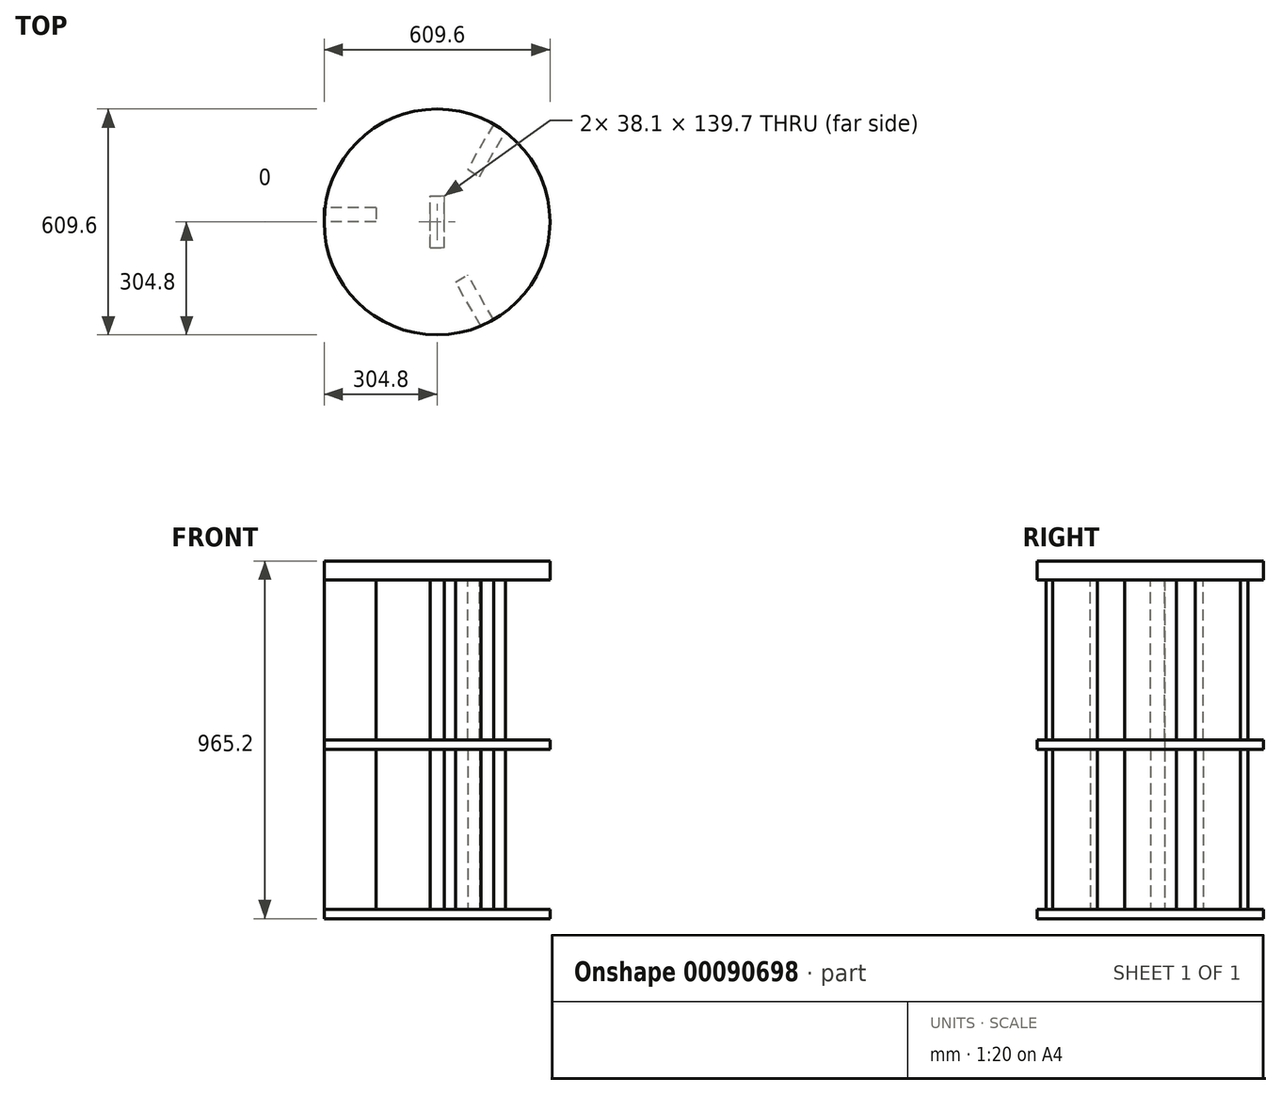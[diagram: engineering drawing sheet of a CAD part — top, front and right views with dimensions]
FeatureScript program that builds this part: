
annotation { "Feature Type Name" : "Feature", "Feature Type Description" : "" }
export const myFeature = defineFeature(function(context is Context, id is Id, definition is map)
    precondition{}
    {
        {
            var Q0;
            Q0=qCreatedBy(makeId("Top.planeOp"),FACE);
            var sketch = newSketch(context, id + "F0", { "sketchPlane" : qUnion([Q0])});
            skCircle(sketch, "E0", {"center": v(0, 0) * mm, "radius": 304.8 * mm});
            skSolve(sketch);
        }
        {
            var Q0;
            Q0 = qSketchRegion(id + "F0", true);
            extrude(context, id + "F1", {"entities" : qUnion([Q0]), "depth" : 25.4 * mm});
        }
        {
            var Q0;
            Q0=qCreatedBy(makeId("Top.planeOp"),FACE);
            cPlane(context, id + "F2", {"entities" : qUnion([Q0]), "cplaneType" : CPlaneType.OFFSET, "offset" : 457.2 * mm, "width" : 152.4 * mm, "height" : 152.4 * mm});
        }
        {
            var Q0;
            Q0=qCreatedBy(id+"F2.planeOp",FACE);
            var sketch = newSketch(context, id + "F3", { "sketchPlane" : qUnion([Q0])});
            skCircle(sketch, "E1", {"center": v(0, 0) * mm, "radius": 304.8 * mm});
            skSolve(sketch);
        }
        {
            var Q0;
            Q0=makeQuery(id+"F3.imprint","IMPRINT",FACE,{"disambiguationData":[TD([[makeQuery(id+"F3.imprint","IMPRINT",EDGE,{"derivedFrom":sQuery(id+"F3.wireOp",EDGE,"E1")}),1.0]])]});
            extrude(context, id + "F4", {"entities" : qUnion([Q0]), "depth" : 25.4 * mm});
        }
        {
            var Q0;
            Q0=qCreatedBy(id+"F2.planeOp",FACE);
            cPlane(context, id + "F5", {"entities" : qUnion([Q0]), "cplaneType" : CPlaneType.OFFSET, "offset" : 457.2 * mm, "width" : 152.4 * mm, "height" : 152.4 * mm});
        }
        {
            var Q0;
            Q0=qCreatedBy(id+"F5.planeOp",FACE);
            var sketch = newSketch(context, id + "F6", { "sketchPlane" : qUnion([Q0])});
            skCircle(sketch, "E2", {"center": v(0, 0) * mm, "radius": 304.8 * mm});
            skSolve(sketch);
        }
        {
            var Q0;
            Q0=makeQuery(id+"F1.opExtrude","CAP_FACE",FACE,{"disambiguationData":[OSD([sQuery(id+"F0.wireOp",EDGE,"E0")])],"isStart":false});
            var sketch = newSketch(context, id + "F7", { "sketchPlane" : qUnion([Q0])});
            skLineSegment(sketch, "E3.bottom", {"start": v(-304.8, 0) * mm, "end": v(-165.1, 0) * mm});
            skLineSegment(sketch, "E3.top", {"start": v(-304.8, 38.1) * mm, "end": v(-165.1, 38.1) * mm});
            skLineSegment(sketch, "E3.left", {"start": v(-304.8, 0) * mm, "end": v(-304.8, 38.1) * mm});
            skLineSegment(sketch, "E3.right", {"start": v(-165.1, 0) * mm, "end": v(-165.1, 38.1) * mm});
            skLineSegment(sketch, "E4", {"start": v(-304.8, 0) * mm, "end": v(0, 0) * mm, "construction": true});
            skLineSegment(sketch, "E5", {"start": v(0, 0) * mm, "end": v(152.4, 263.96) * mm, "construction": true});
            skLineSegment(sketch, "E6", {"start": v(0, 0) * mm, "end": v(152.4, -263.96) * mm, "construction": true});
            skLineSegment(sketch, "E7", {"start": v(82.55, 142.98) * mm, "end": v(152.4, 263.96) * mm});
            skLineSegment(sketch, "E8", {"start": v(184.14, 242.89) * mm, "end": v(114.3, 121.9) * mm});
            skLineSegment(sketch, "E9", {"start": v(114.3, 121.9) * mm, "end": v(82.55, 142.98) * mm});
            skLineSegment(sketch, "E10", {"start": v(152.4, 263.96) * mm, "end": v(184.14, 242.89) * mm});
            skLineSegment(sketch, "E11", {"start": v(82.55, -142.98) * mm, "end": v(49.55, -162.03) * mm});
            skLineSegment(sketch, "E12", {"start": v(49.55, -162.03) * mm, "end": v(118.2, -280.94) * mm});
            skLineSegment(sketch, "E13", {"start": v(118.2, -280.94) * mm, "end": v(152.4, -263.96) * mm});
            skLineSegment(sketch, "E14", {"start": v(82.55, -142.98) * mm, "end": v(152.4, -263.96) * mm});
            skLineSegment(sketch, "E15.bottom", {"start": v(19.05, 69.85) * mm, "end": v(-19.05, 69.85) * mm});
            skLineSegment(sketch, "E15.top", {"start": v(19.05, -69.85) * mm, "end": v(-19.05, -69.85) * mm});
            skLineSegment(sketch, "E15.left", {"start": v(19.05, 69.85) * mm, "end": v(19.05, -69.85) * mm});
            skLineSegment(sketch, "E15.right", {"start": v(-19.05, 69.85) * mm, "end": v(-19.05, -69.85) * mm});
            skPoint(sketch, "E15.middle", {"position": v(0, 0) * mm});
            skSolve(sketch);
        }
        {
            var Q0;
            Q0 = qSketchRegion(id + "F7", true);
            var Q1;
            Q1=makeQuery(id+"F4.opExtrude","CAP_FACE",FACE,{"disambiguationData":[OSD([sQuery(id+"F3.wireOp",EDGE,"E1")])],"isStart":true});
            extrude(context, id + "F8", {"entities" : qUnion([Q0]), "operationType" : NewBodyOperationType.ADD, "endBound" : BoundingType.UP_TO_SURFACE, "endBoundEntityFace" : qUnion([Q1]), "depth" : 25.4 * mm});
        }
        {
            var Q0;
            Q0=makeQuery(id+"F6.imprint","IMPRINT",FACE,{"disambiguationData":[TD([[makeQuery(id+"F6.imprint","IMPRINT",EDGE,{"derivedFrom":sQuery(id+"F6.wireOp",EDGE,"E2")}),1.0]])]});
            var sketch = newSketch(context, id + "F9", { "sketchPlane" : qUnion([Q0])});
            skLineSegment(sketch, "E16.bottom", {"start": v(-304.8, 0) * mm, "end": v(-165.1, 0) * mm});
            skLineSegment(sketch, "E16.top", {"start": v(-304.8, 38.1) * mm, "end": v(-165.1, 38.1) * mm});
            skLineSegment(sketch, "E16.left", {"start": v(-304.8, 0) * mm, "end": v(-304.8, 38.1) * mm});
            skLineSegment(sketch, "E16.right", {"start": v(-165.1, 0) * mm, "end": v(-165.1, 38.1) * mm});
            skLineSegment(sketch, "E17", {"start": v(-304.8, 0) * mm, "end": v(0, 0) * mm, "construction": true});
            skLineSegment(sketch, "E18", {"start": v(0, 0) * mm, "end": v(152.4, 263.96) * mm, "construction": true});
            skLineSegment(sketch, "E19", {"start": v(0, 0) * mm, "end": v(152.4, -263.96) * mm, "construction": true});
            skLineSegment(sketch, "E20", {"start": v(82.55, 142.98) * mm, "end": v(152.4, 263.96) * mm});
            skLineSegment(sketch, "E21", {"start": v(184.14, 242.89) * mm, "end": v(114.3, 121.9) * mm});
            skLineSegment(sketch, "E22", {"start": v(114.3, 121.9) * mm, "end": v(82.55, 142.98) * mm});
            skLineSegment(sketch, "E23", {"start": v(152.4, 263.96) * mm, "end": v(184.14, 242.89) * mm});
            skLineSegment(sketch, "E24", {"start": v(82.55, -142.98) * mm, "end": v(49.55, -162.03) * mm});
            skLineSegment(sketch, "E25", {"start": v(49.55, -162.03) * mm, "end": v(118.2, -280.94) * mm});
            skLineSegment(sketch, "E26", {"start": v(118.2, -280.94) * mm, "end": v(152.4, -263.96) * mm});
            skLineSegment(sketch, "E27", {"start": v(82.55, -142.98) * mm, "end": v(152.4, -263.96) * mm});
            skLineSegment(sketch, "E28.bottom", {"start": v(19.05, 69.85) * mm, "end": v(-19.05, 69.85) * mm});
            skLineSegment(sketch, "E28.top", {"start": v(19.05, -69.85) * mm, "end": v(-19.05, -69.85) * mm});
            skLineSegment(sketch, "E28.left", {"start": v(19.05, 69.85) * mm, "end": v(19.05, -69.85) * mm});
            skLineSegment(sketch, "E28.right", {"start": v(-19.05, 69.85) * mm, "end": v(-19.05, -69.85) * mm});
            skPoint(sketch, "E28.middle", {"position": v(0, 0) * mm});
            skSolve(sketch);
        }
        {
            var Q0;
            Q0 = qSketchRegion(id + "F9", true);
            extrude(context, id + "F10", {"entities" : qUnion([Q0]), "operationType" : NewBodyOperationType.ADD, "endBound" : BoundingType.UP_TO_NEXT, "oppositeDirection" : true, "depth" : 25.4 * mm});
        }
        {
            var Q0;
            Q0=makeQuery(id+"F6.imprint","IMPRINT",FACE,{"disambiguationData":[TD([[makeQuery(id+"F6.imprint","IMPRINT",EDGE,{"derivedFrom":sQuery(id+"F6.wireOp",EDGE,"E2")}),1.0]])]});
            extrude(context, id + "F11", {"entities" : qUnion([Q0]), "operationType" : NewBodyOperationType.ADD, "depth" : 50.8 * mm});
        }
    });
